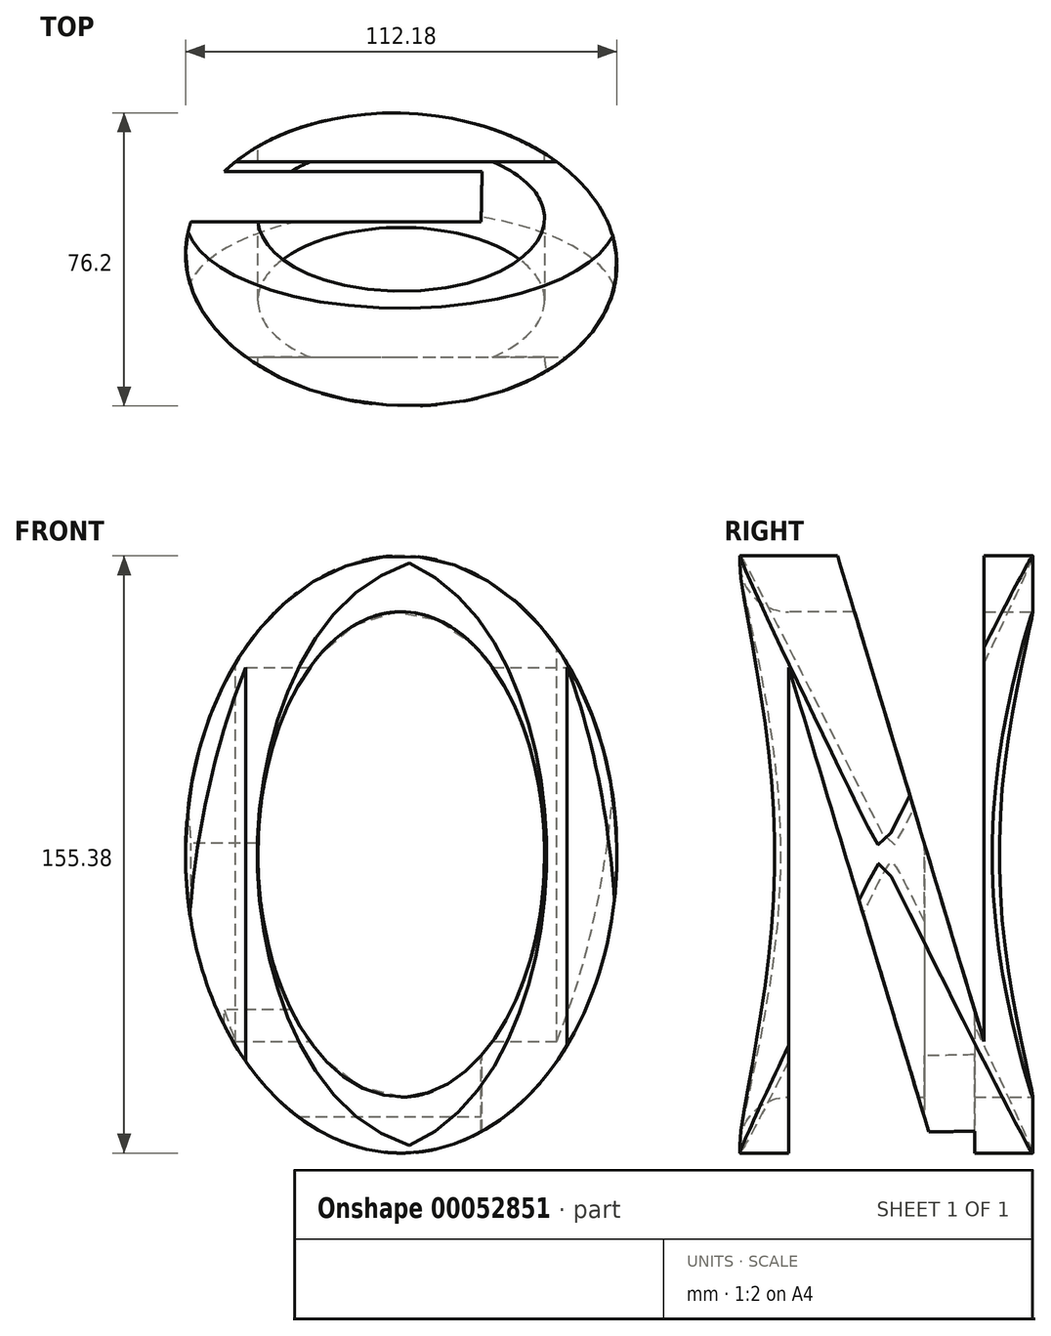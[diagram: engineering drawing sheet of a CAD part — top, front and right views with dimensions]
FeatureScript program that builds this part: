
annotation { "Feature Type Name" : "Feature", "Feature Type Description" : "" }
export const myFeature = defineFeature(function(context is Context, id is Id, definition is map)
    precondition{}
    {
        {
            var Q0;
            Q0=qCreatedBy(makeId("Front.planeOp"),FACE);
            var sketch = newSketch(context, id + "F0", { "sketchPlane" : qUnion([Q0])});
            skEllipse(sketch, "E0", {"center": v(0, 0) * mm, "majorRadius": 37.28 * mm, "minorRadius": 63.12 * mm, "majorAxis": v(-1, 0)});
            skEllipse(sketch, "E1", {"center": v(0, 0) * mm, "majorRadius": 56.1 * mm, "minorRadius": 77.7 * mm, "majorAxis": v(-1, 0)});
            skSolve(sketch);
        }
        {
            var Q0;
            Q0 = qSketchRegion(id + "F0", true);
            extrude(context, id + "F1", {"entities" : qUnion([Q0]), "depth" : 76.2 * mm});
        }
        {
            var Q0;
            Q0=makeQuery(id+"F1.opExtrude","CAP_EDGE",EDGE,{"disambiguationData":[OSD([sQuery(id+"F0.wireOp",EDGE,"E0")])],"isStart":false});
            fillet(context, id + "F2", {"entities" : qUnion([Q0]), "radius" : 12.7 * mm, "tangentPropagation" : true, "allowEdgeOverflow" : false});
        }
        {
            var Q0;
            Q0=qCreatedBy(makeId("Right.planeOp"),FACE);
            var sketch = newSketch(context, id + "F3", { "sketchPlane" : qUnion([Q0])});
            skLineSegment(sketch, "E2", {"start": v(-76.2, -77.7) * mm, "end": v(-76.2, 77.7) * mm});
            skLineSegment(sketch, "E3", {"start": v(-76.2, 77.7) * mm, "end": v(-50.8, 77.7) * mm});
            skLineSegment(sketch, "E4", {"start": v(-50.8, 77.7) * mm, "end": v(-12.7, -48.68) * mm});
            skLineSegment(sketch, "E5", {"start": v(-12.7, -48.68) * mm, "end": v(-12.7, 77.7) * mm});
            skLineSegment(sketch, "E6", {"start": v(-12.7, 77.7) * mm, "end": v(0, 77.7) * mm});
            skLineSegment(sketch, "E7", {"start": v(0, 77.7) * mm, "end": v(0, -77.7) * mm});
            skLineSegment(sketch, "E8", {"start": v(0, -77.7) * mm, "end": v(-25.4, -77.7) * mm});
            skLineSegment(sketch, "E9", {"start": v(-25.4, -77.7) * mm, "end": v(-63.5, 48.68) * mm});
            skLineSegment(sketch, "E10", {"start": v(-63.5, 48.68) * mm, "end": v(-63.5, -77.7) * mm});
            skLineSegment(sketch, "E11", {"start": v(-63.5, -77.7) * mm, "end": v(-76.2, -77.7) * mm});
            skLineSegment(sketch, "E12", {"start": v(0, 0) * mm, "end": v(-76.2, 0) * mm, "construction": true});
            skSolve(sketch);
        }
        {
            var Q0;
            Q0 = qSketchRegion(id + "F3", true);
            extrude(context, id + "F4", {"entities" : qUnion([Q0]), "operationType" : NewBodyOperationType.INTERSECT, "endBound" : BoundingType.THROUGH_ALL, "oppositeDirection" : true, "depth" : 25.4 * mm, "hasSecondDirection" : true, "secondDirectionBound" : SecondDirectionBoundingType.THROUGH_ALL, "secondDirectionOppositeDirection" : false, "secondDirectionDepth" : 25.4 * mm});
        }
        {
            var Q0;
            Q0=qCreatedBy(makeId("Top.planeOp"),FACE);
            var sketch = newSketch(context, id + "F5", { "sketchPlane" : qUnion([Q0])});
            skEllipticalArc(sketch, "E13", {});
            skLineSegment(sketch, "E14", {"start": v(-54.67, -28.25) * mm, "end": v(20.78, -28.25) * mm});
            skLineSegment(sketch, "E15", {"start": v(-46, -15.18) * mm, "end": v(21.02, -15.18) * mm});
            skLineSegment(sketch, "E16", {"start": v(21.02, -15.18) * mm, "end": v(20.78, -28.25) * mm});
            const initialGuessF5  = {"E13": [0, -0.0381, -0.9989456759358435, 0.04590791357925905, 0.056119171185487746, 0.03805291539573125, 6.089346404527909, 5.705333755741661]};
            skSetInitialGuess(sketch, initialGuessF5);
            skSolve(sketch);
        }
        {
            var Q0;
            Q0 = qSketchRegion(id + "F5", true);
            extrude(context, id + "F6", {"entities" : qUnion([Q0]), "operationType" : NewBodyOperationType.INTERSECT, "endBound" : BoundingType.THROUGH_ALL, "oppositeDirection" : true, "depth" : 25.4 * mm, "hasSecondDirection" : true, "secondDirectionBound" : SecondDirectionBoundingType.THROUGH_ALL, "secondDirectionOppositeDirection" : false, "secondDirectionDepth" : 25.4 * mm});
        }
    });
